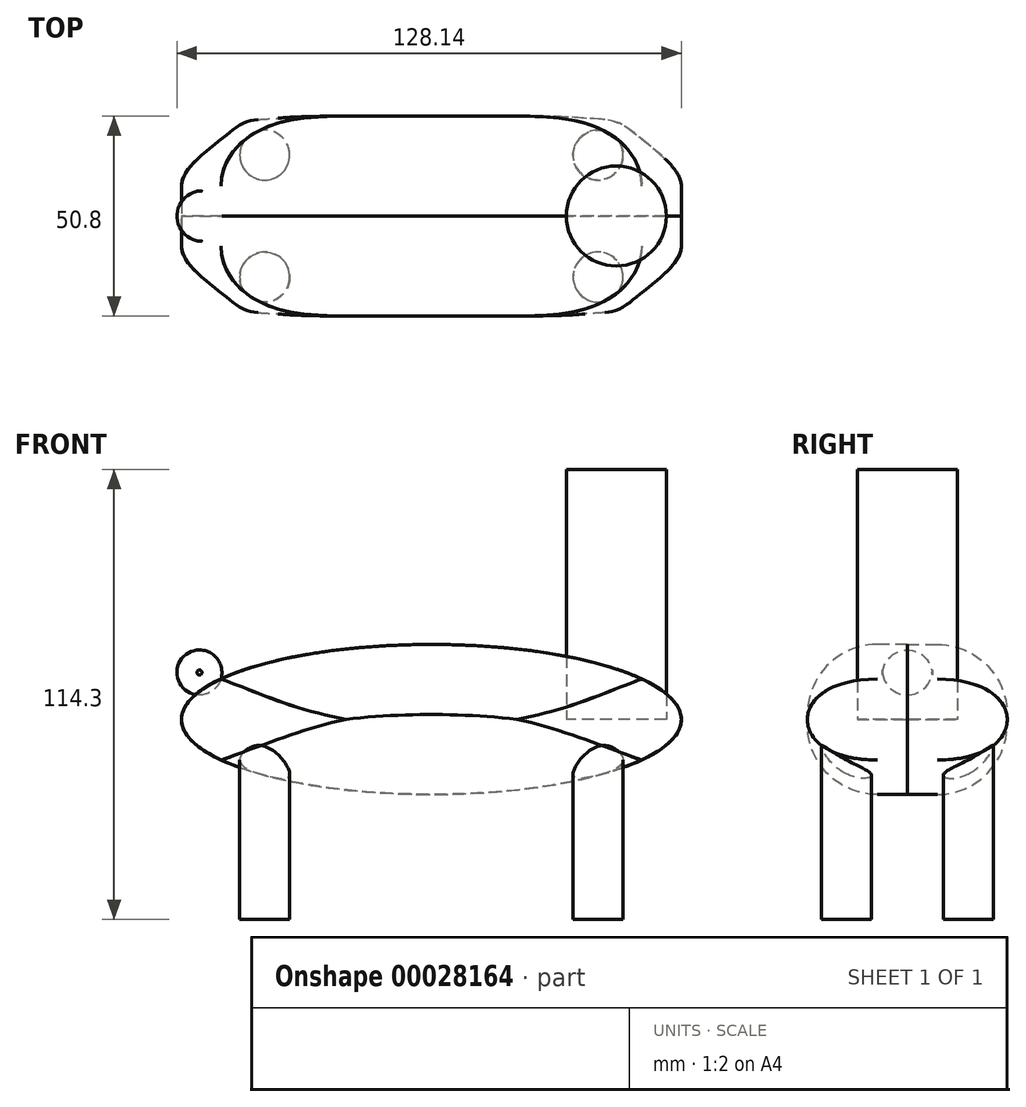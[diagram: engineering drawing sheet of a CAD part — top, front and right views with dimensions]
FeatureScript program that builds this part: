
annotation { "Feature Type Name" : "Feature", "Feature Type Description" : "" }
export const myFeature = defineFeature(function(context is Context, id is Id, definition is map)
    precondition{}
    {
        {
            var Q0;
            Q0=qCreatedBy(makeId("Front.planeOp"),FACE);
            var sketch = newSketch(context, id + "F0", { "sketchPlane" : qUnion([Q0])});
            skEllipse(sketch, "E0", {"center": v(0, 0) * mm, "majorRadius": 63.5 * mm, "minorRadius": 19.05 * mm, "majorAxis": v(1, 0)});
            skSolve(sketch);
        }
        {
            var Q0;
            Q0 = qSketchRegion(id + "F0", true);
            extrude(context, id + "F1", {"entities" : qUnion([Q0]), "depth" : 25.4 * mm});
        }
        {
            var Q0;
            Q0=makeQuery(id+"F1.opExtrude","CAP_EDGE",EDGE,{"disambiguationData":[OSD([sQuery(id+"F0.wireOp",EDGE,"E0")])],"isStart":false});
            fillet(context, id + "F2", {"entities" : qUnion([Q0]), "radius" : 17.78 * mm, "tangentPropagation" : true, "allowEdgeOverflow" : false});
        }
        {
            var Q0;
            Q0=makeQuery(id+"F1.opExtrude","SWEPT_BODY",BODY,{"disambiguationData":[OSD([sQuery(id+"F0.wireOp",EDGE,"E0")])]});
            var Q1;
            Q1=qCreatedBy(makeId("Front.planeOp"),FACE);
            mirror(context, id + "F3", {"entities" : qUnion([Q0]), "mirrorPlane" : qUnion([Q1])});
        }
        {
            var Q0;
            Q0=qCreatedBy(makeId("Front.planeOp"),FACE);
            var sketch = newSketch(context, id + "F4", { "sketchPlane" : qUnion([Q0])});
            skCircle(sketch, "E1", {"center": v(-58.93, 11.94) * mm, "radius": 6.99 * mm});
            skSolve(sketch);
        }
        {
            var Q0;
            Q0=makeQuery(id+"F4.imprint","IMPRINT",FACE,{"disambiguationData":[TD([[makeQuery(id+"F4.imprint","IMPRINT",EDGE,{"derivedFrom":sQuery(id+"F4.wireOp",EDGE,"E1")}),1.0]])]});
            extrude(context, id + "F5", {"entities" : qUnion([Q0]), "endBound" : BoundingType.SYMMETRIC, "depth" : 12.7 * mm});
        }
        {
            var Q0;
            Q0=makeQuery(id+"F5.opExtrude","CAP_FACE",FACE,{"disambiguationData":[OSD([sQuery(id+"F4.wireOp",EDGE,"E1")])],"isStart":false});
            fillet(context, id + "F6", {"entities" : qUnion([Q0]), "radius" : 6.35 * mm, "tangentPropagation" : true, "allowEdgeOverflow" : false});
        }
        {
            var Q0;
            Q0=makeQuery(id+"F5.opExtrude","CAP_FACE",FACE,{"disambiguationData":[OSD([sQuery(id+"F4.wireOp",EDGE,"E1")])],"isStart":true});
            fillet(context, id + "F7", {"entities" : qUnion([Q0]), "radius" : 6.35 * mm, "tangentPropagation" : true, "allowEdgeOverflow" : false});
        }
        {
            var Q0;
            Q0=qCreatedBy(makeId("Top.planeOp"),FACE);
            var sketch = newSketch(context, id + "F8", { "sketchPlane" : qUnion([Q0])});
            skCircle(sketch, "E2", {"center": v(-42.34, -15.49) * mm, "radius": 6.35 * mm});
            skSolve(sketch);
        }
        {
            var Q0;
            Q0 = qSketchRegion(id + "F8", true);
            extrude(context, id + "F9", {"entities" : qUnion([Q0]), "operationType" : NewBodyOperationType.ADD, "oppositeDirection" : true, "depth" : 50.8 * mm});
        }
        {
            var Q0;
            Q0=makeQuery(id+"F1.opExtrude","SWEPT_BODY",BODY,{"disambiguationData":[OSD([sQuery(id+"F0.wireOp",EDGE,"E0")])]});
            var Q1;
            Q1=qCreatedBy(makeId("Front.planeOp"),FACE);
            mirror(context, id + "F10", {"entities" : qUnion([Q0]), "mirrorPlane" : qUnion([Q1])});
        }
        {
            var Q0;
            Q0=makeQuery(id+"F1.opExtrude","SWEPT_BODY",BODY,{"disambiguationData":[OSD([sQuery(id+"F0.wireOp",EDGE,"E0")])]});
            var Q1;
            Q1=makeQuery(id+"F10.opPattern","COPY",BODY,{"derivedFrom":makeQuery(id+"F1.opExtrude","SWEPT_BODY",BODY,{"disambiguationData":[OSD([sQuery(id+"F0.wireOp",EDGE,"E0")])]}),"instanceName":"1"});
            var Q2;
            Q2=qCreatedBy(makeId("Right.planeOp"),FACE);
            mirror(context, id + "F11", {"entities" : qUnion([Q0, Q1]), "mirrorPlane" : qUnion([Q2])});
        }
        {
            var Q0;
            Q0=qCreatedBy(makeId("Top.planeOp"),FACE);
            var sketch = newSketch(context, id + "F12", { "sketchPlane" : qUnion([Q0])});
            skCircle(sketch, "E3", {"center": v(47, 0) * mm, "radius": 12.7 * mm});
            skSolve(sketch);
        }
        {
            var Q0;
            Q0 = qSketchRegion(id + "F12", true);
            extrude(context, id + "F13", {"entities" : qUnion([Q0]), "depth" : 63.5 * mm});
        }
    });
